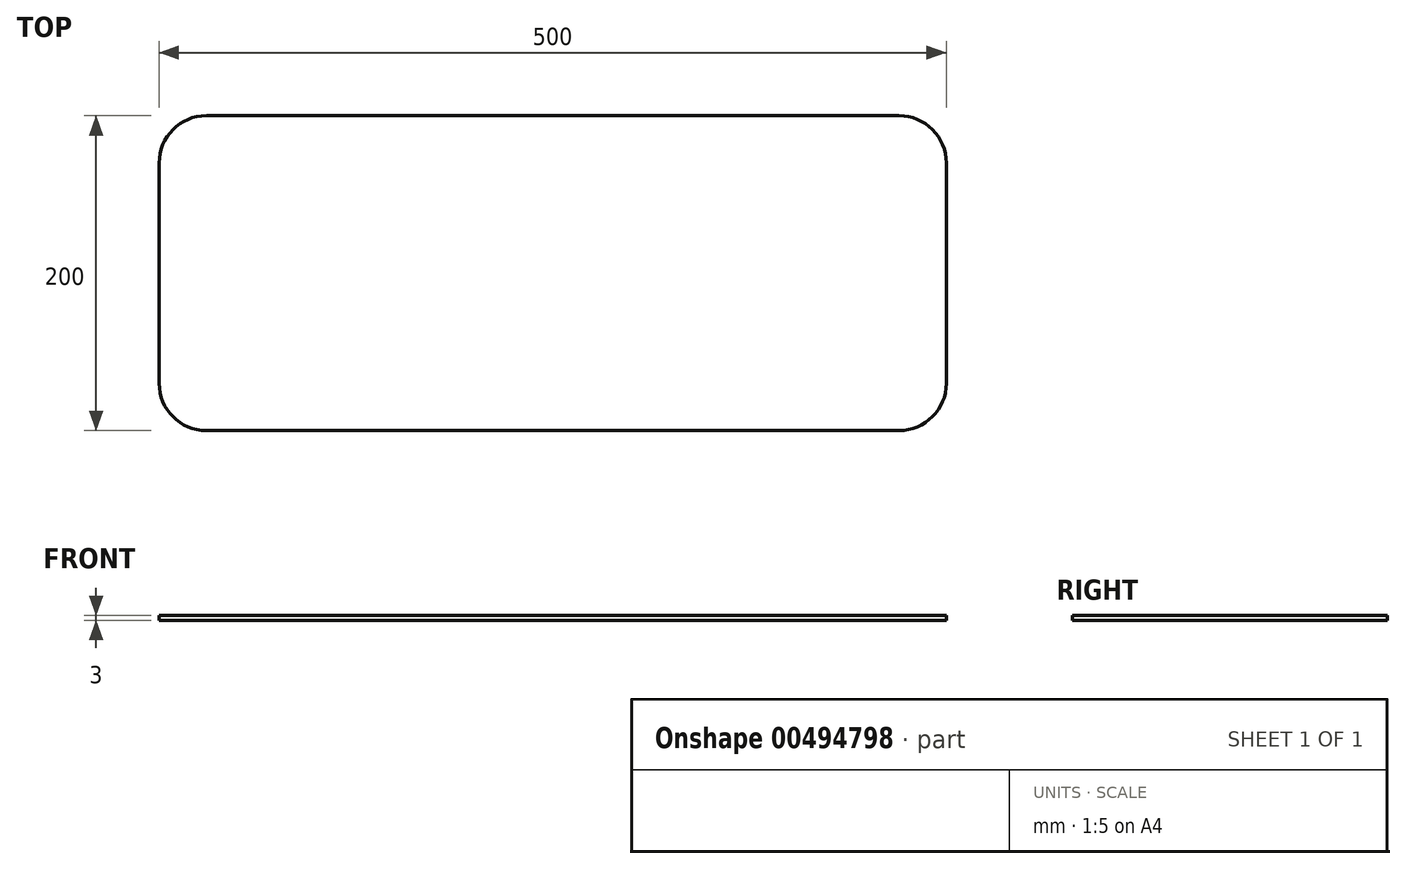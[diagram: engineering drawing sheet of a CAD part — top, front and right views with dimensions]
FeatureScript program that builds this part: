
annotation { "Feature Type Name" : "Feature", "Feature Type Description" : "" }
export const myFeature = defineFeature(function(context is Context, id is Id, definition is map)
    precondition{}
    {
        {
            var Q0;
            Q0=qCreatedBy(makeId("Top.planeOp"),FACE);
            var sketch = newSketch(context, id + "F0", { "sketchPlane" : qUnion([Q0])});
            skLineSegment(sketch, "E0.bottom", {"start": v(250, -100) * mm, "end": v(-250, -100) * mm});
            skLineSegment(sketch, "E0.top", {"start": v(250, 100) * mm, "end": v(-250, 100) * mm});
            skLineSegment(sketch, "E0.left", {"start": v(250, -100) * mm, "end": v(250, 100) * mm});
            skLineSegment(sketch, "E0.right", {"start": v(-250, -100) * mm, "end": v(-250, 100) * mm});
            skPoint(sketch, "E0.middle", {"position": v(0, 0) * mm});
            skSolve(sketch);
        }
        {
            var Q0;
            Q0=qSketchRegion(id+"F0",true);
            extrude(context, id + "F1", {"entities" : qUnion([Q0]), "depth" : 3 * mm});
        }
        {
            var Q0;
            Q0=makeQuery(id+"F1.opExtrude","SWEPT_EDGE",EDGE,{"disambiguationData":[OSD([sQuery(id+"F0.wireOp",EDGE,"E0.bottom"),sQuery(id+"F0.wireOp",EDGE,"E0.right")])]});
            var Q1;
            Q1=makeQuery(id+"F1.opExtrude","SWEPT_EDGE",EDGE,{"disambiguationData":[OSD([sQuery(id+"F0.wireOp",EDGE,"E0.top"),sQuery(id+"F0.wireOp",EDGE,"E0.left")])]});
            var Q2;
            Q2=makeQuery(id+"F1.opExtrude","SWEPT_EDGE",EDGE,{"disambiguationData":[OSD([sQuery(id+"F0.wireOp",EDGE,"E0.top"),sQuery(id+"F0.wireOp",EDGE,"E0.right")])]});
            var Q3;
            Q3=makeQuery(id+"F1.opExtrude","SWEPT_EDGE",EDGE,{"disambiguationData":[OSD([sQuery(id+"F0.wireOp",EDGE,"E0.bottom"),sQuery(id+"F0.wireOp",EDGE,"E0.left")])]});
            fillet(context, id + "F2", {"entities" : qUnion([Q0, Q1, Q2, Q3]), "radius" : 30 * mm, "tangentPropagation" : true, "allowEdgeOverflow" : false});
        }
    });
